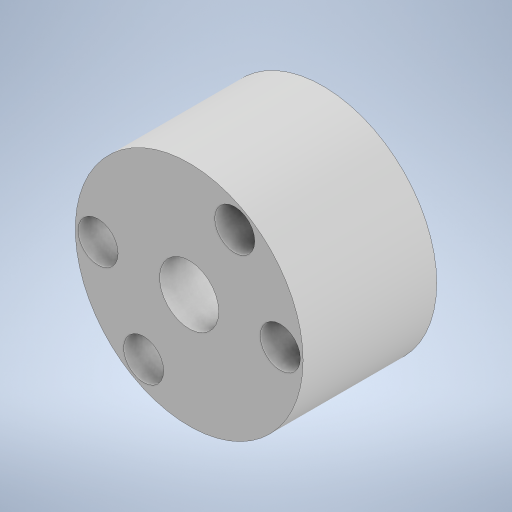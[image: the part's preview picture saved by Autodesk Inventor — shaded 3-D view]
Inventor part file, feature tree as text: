
AUTODESK INVENTOR PART (.ipt)
format: ipt  version: 2023 (Build 270158000, 158)  size: 257,536 bytes
history: native  units: in
note: dims shown in document units (in); Inventor stores cm internally (conversion verified against a paired STEP export)
features: extrude x1, sketch x1
ambient origin geometry x8: Origin, YZ Plane, XZ Plane, XY Plane, X Axis, Y Axis, Z Axis, Center Point
bodies: Body1 (feature_tree)
feature tree (2):
  extrude  "Extrusion14"  Depth=0.44in
  sketch  "Sketch1"  dims[d3=0.866in d15=0.75in d37=0.75in d69=0.132in d70=0.132in d73=0.44in d74=0.0in d75=0.132in d76=0.132in d79=0.3in d80=0.3in d82=0.195in d83=0.3in d84=0.3in d85=0.132in d86=0.132in d87=0.132in d88=0.132in d89=0.3in d90=0.3in d91=0.195in d92=0.3in d93=0.3in]
